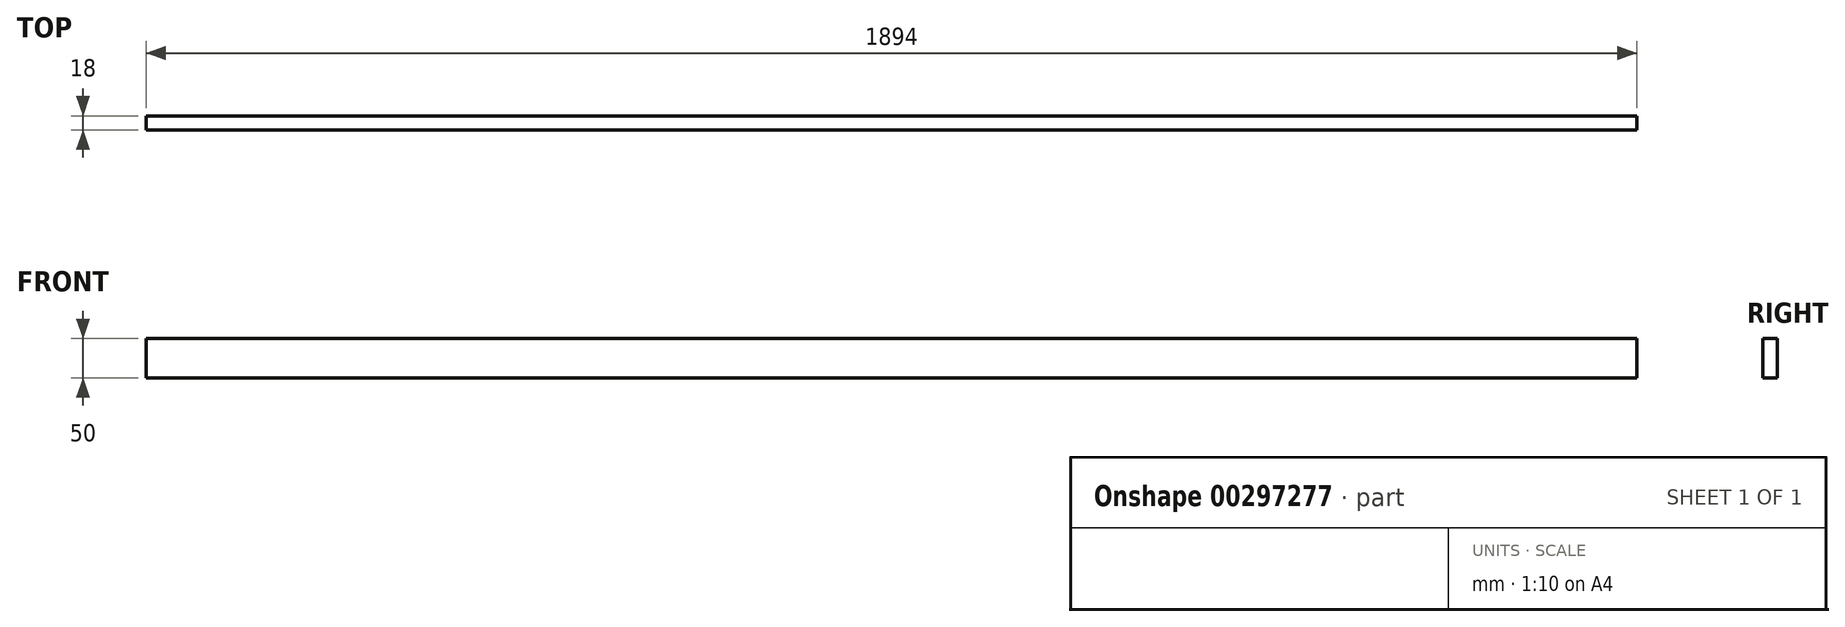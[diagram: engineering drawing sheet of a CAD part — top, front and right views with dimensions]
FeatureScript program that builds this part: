
annotation { "Feature Type Name" : "Feature", "Feature Type Description" : "" }
export const myFeature = defineFeature(function(context is Context, id is Id, definition is map)
    precondition{}
    {
        {
            var Q0;
            Q0=qCreatedBy(makeId("Right.planeOp"),FACE);
            var sketch = newSketch(context, id + "F0", { "sketchPlane" : qUnion([Q0])});
            skLineSegment(sketch, "E0.bottom", {"start": v(9, 25) * mm, "end": v(-9, 25) * mm});
            skLineSegment(sketch, "E0.top", {"start": v(9, -25) * mm, "end": v(-9, -25) * mm});
            skLineSegment(sketch, "E0.left", {"start": v(9, 25) * mm, "end": v(9, -25) * mm});
            skLineSegment(sketch, "E0.right", {"start": v(-9, 25) * mm, "end": v(-9, -25) * mm});
            skPoint(sketch, "E0.middle", {"position": v(0, 0) * mm});
            skSolve(sketch);
        }
        {
            var Q0;
            Q0 = qSketchRegion(id + "F0", true);
            extrude(context, id + "F1", {"entities" : qUnion([Q0]), "depth" : 1894 * mm});
        }
    });
